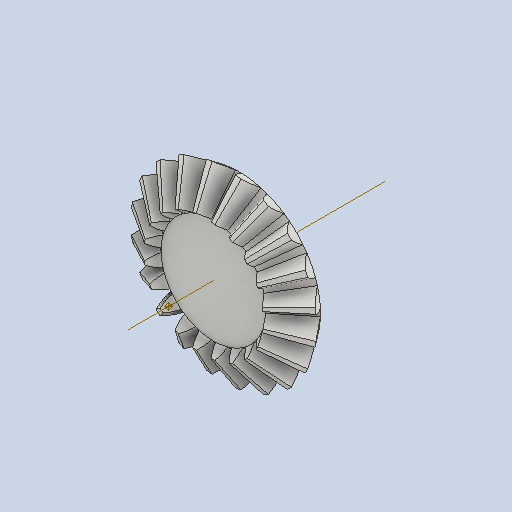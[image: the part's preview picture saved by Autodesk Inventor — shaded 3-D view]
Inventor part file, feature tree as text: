
AUTODESK INVENTOR PART (.ipt)
format: ipt  version: 2025.2 (Build 292293000, 293)  size: 463,360 bytes
history: native  units: mm
features: other x24, loft x2, pattern_circular x2
ambient origin geometry x6: Origin, XZ Plane, X Axis, Y Axis, Z Axis, Center Point
bodies: Solid1 (feature_tree)
feature tree (28):
  other  "Top Point"
  other  "Mesh Plane2"
  other  "Teeth Body"
  other  "Start Point"
  other  "Tooth Plane"
  other  "Start Sketch"
  other  "End Point"
  other  "3D Sketch Right"
  other  "End Plane Right"
  loft  "Loft Right"
  pattern_circular  "Circular Pattern Right"  [2 undecoded]
  other  "3D Sketch Left"
  other  "End Plane Left"
  loft  "Loft Left"
  pattern_circular  "Circular Pattern Left"  [2 undecoded]
  other  "Fix Body"
  other  "Mesh Plane"
  other  "Top Plane"
  other  "Teeth Body Sketch"
  other  "End Plane"
  other  "End Sketch"
  other  "Helical Curve Left"
  other  "End Sketch Left"
  other  "Body Sketch"
  other  "Srf1"
  other  "Helical Curve Right"
  other  "End Sketch Right"
  other  "Pitch Diameter"
note: 4 required parameter values undecoded (feature->parameter linkage not recoverable at this tier; creation-order binding heuristic only, values carry confidence <= 0.55)
